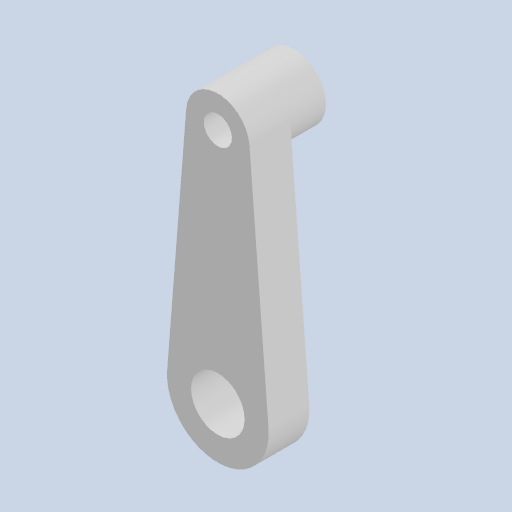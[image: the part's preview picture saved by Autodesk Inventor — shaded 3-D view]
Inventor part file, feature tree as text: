
AUTODESK INVENTOR PART (.ipt)
format: ipt  version: 2022 (Build 260153000, 153)  size: 133,632 bytes
history: native  units: mm
features: other x8, reference x4, extrude x2, sketch x2, projected_geometry x1
ambient origin geometry x8: Origin, YZ Plane, XZ Plane, XY Plane, X Axis, Y Axis, Z Axis, Center Point
bodies: Body1 (feature_tree)
feature tree (17):
  other  "Твердое тело1"
  extrude  "Выдавливание1"  Depth=3.2mm
  extrude  "Выдавливание2"  Depth=4.2mm
  sketch  "Эскиз1"
  reference  "Ссылка1"
  reference  "Ссылка2"
  sketch  "Эскиз2"
  reference  "Ссылка3"
  reference  "Ссылка4"
  projected_geometry  "Спроецированная петля1"
  other  "<userpath>\Documents\Git\MZCAT_2024\MZCAT_2.iam"
  other  "MZCAT_2.iam"
  other  "vzuh_karetka:1"
  other  "<userpath>\Documents\Git\MZCAT_2024\MZCAT.iam"
  other  "MZCAT.iam"
  other  "shatun_main:1"
  other  "plan:1"
